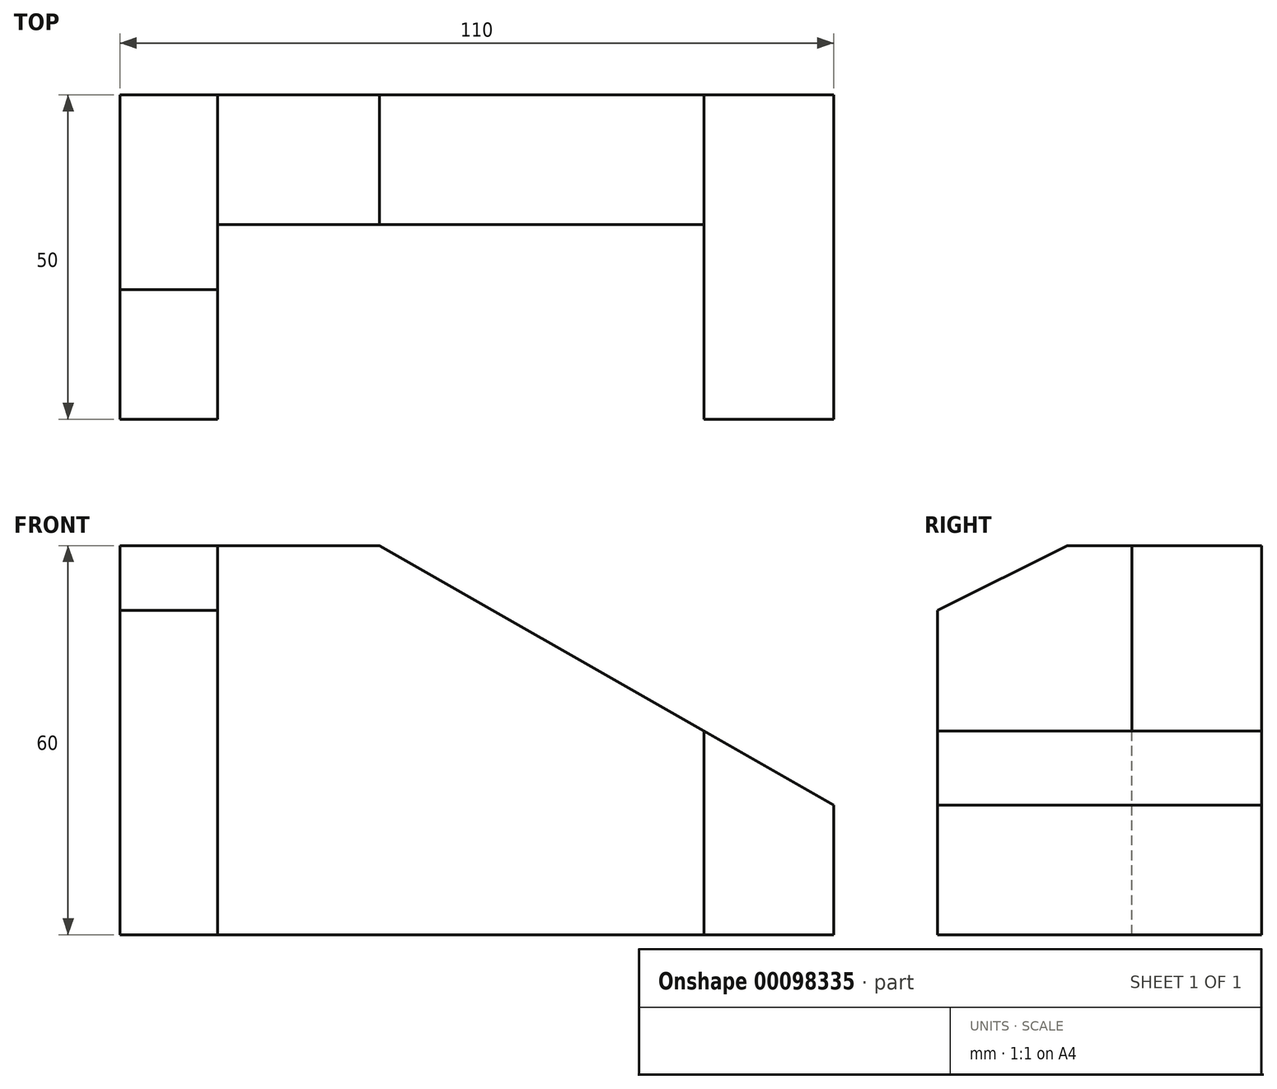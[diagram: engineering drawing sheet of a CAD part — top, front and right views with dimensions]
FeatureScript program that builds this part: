
annotation { "Feature Type Name" : "Feature", "Feature Type Description" : "" }
export const myFeature = defineFeature(function(context is Context, id is Id, definition is map)
    precondition{}
    {
        {
            var Q0;
            Q0=qCreatedBy(makeId("Front.planeOp"),FACE);
            var sketch = newSketch(context, id + "F0", { "sketchPlane" : qUnion([Q0])});
            skLineSegment(sketch, "E0", {"start": v(0, 0) * mm, "end": v(110, 0) * mm});
            skLineSegment(sketch, "E1", {"start": v(110, 0) * mm, "end": v(110, 20) * mm});
            skLineSegment(sketch, "E2", {"start": v(110, 20) * mm, "end": v(40, 60) * mm});
            skLineSegment(sketch, "E3", {"start": v(40, 60) * mm, "end": v(0, 60) * mm});
            skLineSegment(sketch, "E4", {"start": v(0, 60) * mm, "end": v(0, 0) * mm});
            skLineSegment(sketch, "E5", {"start": v(15, 0) * mm, "end": v(15, 60) * mm});
            skLineSegment(sketch, "E6", {"start": v(90, 0) * mm, "end": v(90, 31.43) * mm});
            skSolve(sketch);
        }
        {
            var Q0;
            {var subQ0=sQuery(id+"F0.wireOp",EDGE,"E4");Q0=makeQuery(id+"F0.imprint","IMPRINT",FACE,{"disambiguationData":[TD([[makeQuery(id+"F0.imprint","IMPRINT",EDGE,{"derivedFrom":subQ0}),1.0]])]});}
            var Q1;
            {var subQ0=sQuery(id+"F0.wireOp",EDGE,"E1");Q1=makeQuery(id+"F0.imprint","IMPRINT",FACE,{"disambiguationData":[TD([[makeQuery(id+"F0.imprint","IMPRINT",EDGE,{"derivedFrom":subQ0}),1.0]])]});}
            var Q2;
            {var subQ0=sQuery(id+"F0.wireOp",EDGE,"E4");Q2=makeQuery(id+"F0.imprint","IMPRINT",FACE,{"disambiguationData":[TD([[makeQuery(id+"F0.imprint","IMPRINT",EDGE,{"derivedFrom":subQ0}),1.0]])]});}
            var Q3;
            {var subQ0=sQuery(id+"F0.wireOp",EDGE,"E1");Q3=makeQuery(id+"F0.imprint","IMPRINT",FACE,{"disambiguationData":[TD([[makeQuery(id+"F0.imprint","IMPRINT",EDGE,{"derivedFrom":subQ0}),1.0]])]});}
            extrude(context, id + "F1", {"entities" : qUnion([Q0, Q1, Q2, Q3]), "depth" : 50 * mm});
        }
        {
            var Q0;
            {var subQ0=sQuery(id+"F0.wireOp",EDGE,"E5");Q0=makeQuery(id+"F0.imprint","IMPRINT",FACE,{"disambiguationData":[TD([[makeQuery(id+"F0.imprint","IMPRINT",EDGE,{"derivedFrom":subQ0}),-1.0]])]});}
            extrude(context, id + "F2", {"entities" : qUnion([Q0]), "depth" : 20 * mm});
        }
        {
            var Q0;
            Q0=makeQuery(id+"F1.opExtrude","SWEPT_FACE",FACE,{"disambiguationData":[OSD([sQuery(id+"F0.wireOp",EDGE,"E5")])]});
            var sketch = newSketch(context, id + "F3", { "sketchPlane" : qUnion([Q0])});
            skLineSegment(sketch, "E7", {"start": v(-50, 50) * mm, "end": v(-30, 60) * mm});
            skSolve(sketch);
        }
        {
            var Q0;
            Q0 = qSketchRegion(id + "F3", true);
            var Q1;
            {var subQ0=sQuery(id+"F3.wireOp",EDGE,"E7");Q1=makeQuery(id+"F3.imprint","IMPRINT",FACE,{"disambiguationData":[TD([[makeQuery(id+"F3.imprint","IMPRINT",EDGE,{"derivedFrom":subQ0}),1.0]])]});}
            extrude(context, id + "F4", {"entities" : qUnion([Q0, Q1]), "operationType" : NewBodyOperationType.REMOVE, "oppositeDirection" : true, "depth" : 15 * mm});
        }
    });
